# Revit family: Accessories-Teknion-HWBECMT_hiSpace_120_Cable_Riser_Mid-R2020
name_source: partatom
category: Furniture
units: mm (PartAtom-declared; Revit-internal decimal feet)

## family parameters
Always vertical = Yes
Cut with Voids When Loaded = No
OmniClass Number = 23.40.20.00
OmniClass Title = General Furniture and Specialties
Room Calculation Point = No
Shared = Yes
Work Plane-Based = No

## types (3) — shared parameters
Assembly Code = E2020200
Manufacturer = Teknion
Manufacturer Fax = 416.661.4586
Part Number = HWBECMT
Product Documentation Link = https://www.teknion.com
Product Line = hiSpace 120 Bench
Product Page URL = https://www.teknion.com
Series = Height-Adjustable Bench hiSpace
Sustainability Data = https://www.teknion.com
URL = www.teknion.com
Unit Weight URL = http://www.teknion.com
Warranty = http://www.teknion.com
zero-valued in all types: Default Elevation

## per-type parameters (varying)
| type | Cover Finish | Description | Model |
| 52 Ebony | Paint - Teknion - 52 - Ebony | hiSpace 120 Cable Riser - Mid - Ebony (52) Finish | HWBECMT52 |
| 60 Platinum | Paint - Teknion - Mica - Platinum | hiSpace 120 Cable Riser - Mid - Platinum (60) Finish | HWBECMT60 |
| 83 Very White | Paint  -Teknion - 83 - Very White | hiSpace 120 Cable Riser - Mid - Very White (83) Finish | HWBECMT83 |

## geometry (parser evidence)
native form markers: Sweep x3
no freeform markers — native parametric forms only
